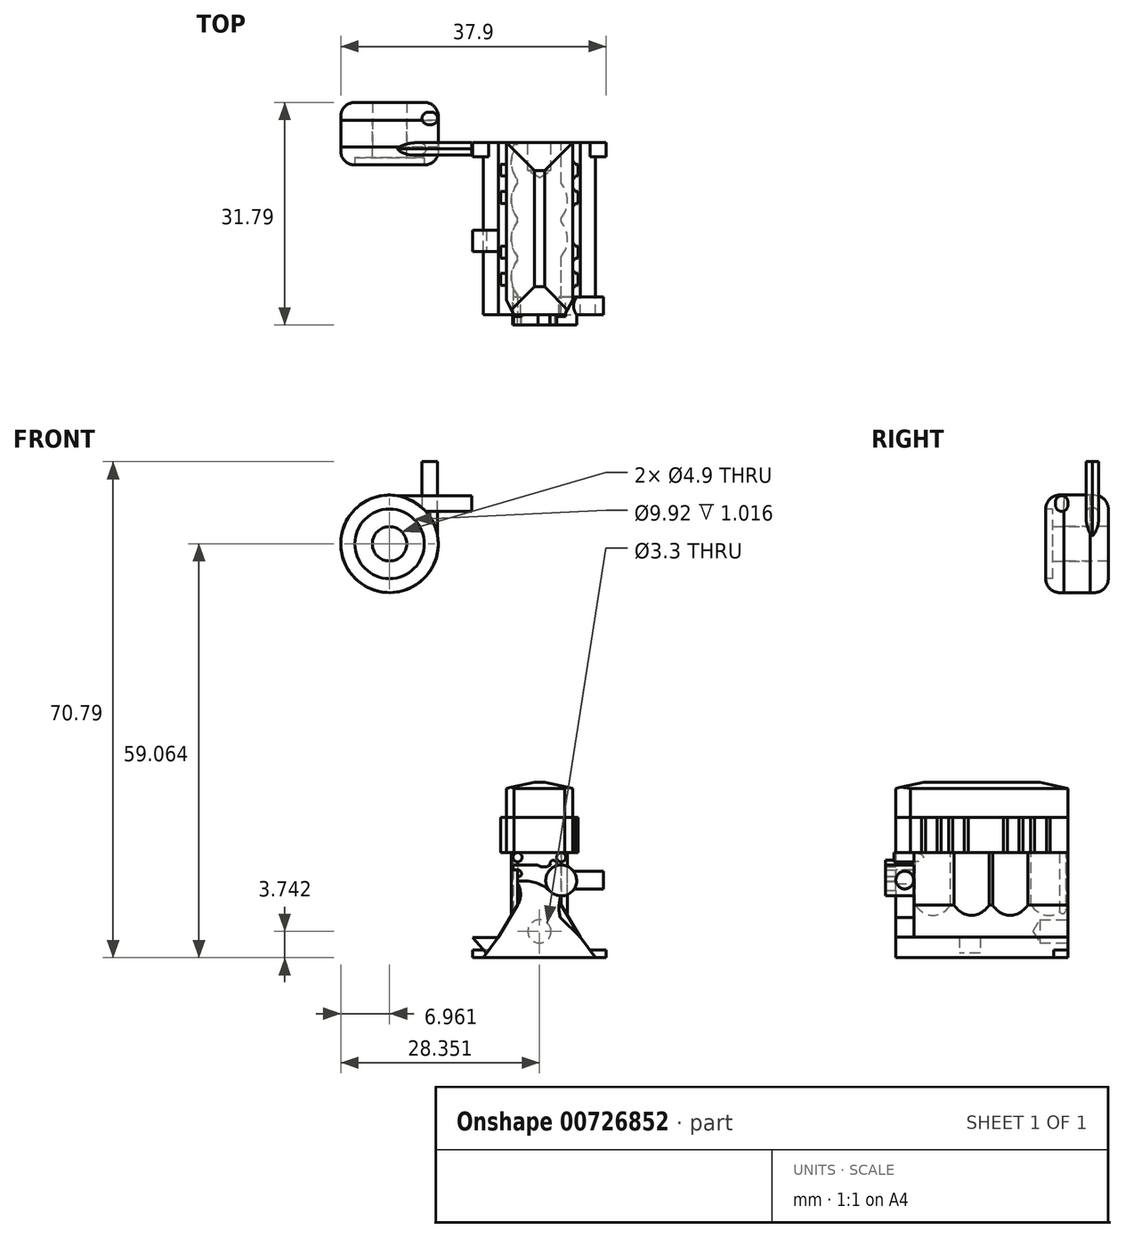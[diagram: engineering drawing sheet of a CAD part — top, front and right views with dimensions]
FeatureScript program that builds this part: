
annotation { "Feature Type Name" : "Feature", "Feature Type Description" : "" }
export const myFeature = defineFeature(function(context is Context, id is Id, definition is map)
    precondition{}
    {
        {
            var Q0;
            Q0=qCreatedBy(makeId("Front.planeOp"),FACE);
            var sketch = newSketch(context, id + "F0", { "sketchPlane" : qUnion([Q0])});
            skLineSegment(sketch, "E0.bottom", {"start": v(-2.64, 0.8) * mm, "end": v(3.58, 0.8) * mm});
            skLineSegment(sketch, "E0.top", {"start": v(-2.64, -6.71) * mm, "end": v(3.58, -6.71) * mm});
            skLineSegment(sketch, "E0.left", {"start": v(-2.64, 0.8) * mm, "end": v(-2.64, -6.71) * mm});
            skLineSegment(sketch, "E0.right", {"start": v(3.58, 0.8) * mm, "end": v(3.58, -6.71) * mm});
            skLineSegment(sketch, "E1", {"start": v(-2.64, -6.71) * mm, "end": v(-5.38, -11.28) * mm});
            skPoint(sketch, "E2", {"position": v(0.47, -6.71) * mm});
            skLineSegment(sketch, "E3.MirrorCS", {"start": v(3.58, -6.71) * mm, "end": v(6.32, -11.28) * mm});
            skLineSegment(sketch, "E4", {"start": v(-5.38, -11.28) * mm, "end": v(-7.54, -14.2) * mm});
            skLineSegment(sketch, "E5.MirrorCS", {"start": v(6.32, -11.28) * mm, "end": v(8.48, -14.2) * mm});
            skLineSegment(sketch, "E6", {"start": v(-7.54, -14.2) * mm, "end": v(8.48, -14.2) * mm});
            skLineSegment(sketch, "E7", {"start": v(7.69, -13.13) * mm, "end": v(10.02, -13.13) * mm});
            skLineSegment(sketch, "E8", {"start": v(10.02, -13.13) * mm, "end": v(10.02, -14.2) * mm});
            skLineSegment(sketch, "E9", {"start": v(10.02, -14.2) * mm, "end": v(8.48, -14.2) * mm});
            skLineSegment(sketch, "E10.MirrorCS", {"start": v(-6.74, -13.13) * mm, "end": v(-9.08, -13.13) * mm});
            skLineSegment(sketch, "E11.MirrorCS", {"start": v(-9.08, -13.13) * mm, "end": v(-9.08, -14.2) * mm});
            skLineSegment(sketch, "E12.MirrorCS", {"start": v(-9.08, -14.2) * mm, "end": v(-7.54, -14.2) * mm});
            skSolve(sketch);
        }
        {
            var Q0;
            Q0=makeQuery(id+"F0.imprint","IMPRINT",FACE,{"disambiguationData":[TD([[makeQuery(id+"F0.imprint","IMPRINT",EDGE,{"derivedFrom":sQuery(id+"F0.wireOp",EDGE,"E0.bottom")}),-1.0]])]});
            var Q1;
            Q1=makeQuery(id+"F0.imprint","IMPRINT",FACE,{"disambiguationData":[TD([[makeQuery(id+"F0.imprint","IMPRINT",EDGE,{"derivedFrom":sQuery(id+"F0.wireOp",EDGE,"E0.top")}),-1.0]])]});
            extrude(context, id + "F1", {"entities" : qUnion([Q0, Q1]), "depth" : 22 * mm, "offsetDistance" : 25.4 * mm});
        }
        {
            var Q0;
            {var subQ2=sQuery(id+"F0.wireOp",EDGE,"E7");Q0=makeQuery(id+"F0.imprint","IMPRINT",FACE,{"disambiguationData":[TD([[makeQuery(id+"F0.imprint","IMPRINT",EDGE,{"derivedFrom":subQ2}),-1.0]])]});}
            var Q1;
            {var subQ2=sQuery(id+"F0.wireOp",EDGE,"E10.MirrorCS");Q1=makeQuery(id+"F0.imprint","IMPRINT",FACE,{"disambiguationData":[TD([[makeQuery(id+"F0.imprint","IMPRINT",EDGE,{"derivedFrom":subQ2}),1.0]])]});}
            extrude(context, id + "F2", {"entities" : qUnion([Q0, Q1]), "operationType" : NewBodyOperationType.ADD, "depth" : 2 * mm, "offsetDistance" : 25.4 * mm});
        }
        {
            var Q0;
            Q0=makeQuery(id+"F1.opExtrude","SWEPT_FACE",FACE,{"disambiguationData":[OSD([sQuery(id+"F0.wireOp",EDGE,"E0.bottom")])]});
            var sketch = newSketch(context, id + "F3", { "sketchPlane" : qUnion([Q0])});
            skPoint(sketch, "E13", {"position": v(3.58, -11) * mm});
            skLineSegment(sketch, "E14", {"start": v(3.58, 0) * mm, "end": v(3.58, -11) * mm});
            skLineSegment(sketch, "E15", {"start": v(3.58, -11) * mm, "end": v(3.58, -22) * mm});
            skPoint(sketch, "E16", {"position": v(3.58, -16.5) * mm});
            skPoint(sketch, "E17", {"position": v(3.58, -5.5) * mm});
            skLineSegment(sketch, "E18", {"start": v(3.58, -5.5) * mm, "end": v(-2.64, -5.5) * mm});
            skLineSegment(sketch, "E19", {"start": v(-2.64, 0) * mm, "end": v(-2.64, -5.5) * mm});
            skLineSegment(sketch, "E20", {"start": v(-2.64, 0) * mm, "end": v(3.58, 0) * mm});
            skLineSegment(sketch, "E21", {"start": v(-2.64, -5.5) * mm, "end": v(-2.64, -22) * mm});
            skLineSegment(sketch, "E22", {"start": v(-2.64, -22) * mm, "end": v(3.58, -22) * mm});
            skLineSegment(sketch, "E23", {"start": v(3.58, -11) * mm, "end": v(-2.64, -11) * mm});
            skLineSegment(sketch, "E24", {"start": v(3.58, -16.5) * mm, "end": v(-2.64, -16.5) * mm});
            skPoint(sketch, "E25", {"position": v(0.47, -5.5) * mm});
            skLineSegment(sketch, "E26", {"start": v(0.47, 0) * mm, "end": v(0.47, -5.5) * mm});
            skLineSegment(sketch, "E27", {"start": v(0.47, -11) * mm, "end": v(0.47, -5.5) * mm});
            skLineSegment(sketch, "E28", {"start": v(0.47, -11) * mm, "end": v(0.47, -16.5) * mm});
            skLineSegment(sketch, "E29", {"start": v(0.47, -16.5) * mm, "end": v(0.47, -22) * mm});
            skPoint(sketch, "E30", {"position": v(0.47, -19.25) * mm});
            skPoint(sketch, "E31", {"position": v(0.47, -13.75) * mm});
            skPoint(sketch, "E32", {"position": v(0.47, -8.25) * mm});
            skPoint(sketch, "E33", {"position": v(0.47, -2.75) * mm});
            skArc(sketch, "E34", {"start": v(-2.43, 0) * mm, "mid": v(0.47, -6.75) * mm, "end": v(3.38, 0) * mm});
            skCircle(sketch, "E35", {"center": v(0.47, -8.25) * mm, "radius": 4 * mm});
            skCircle(sketch, "E36", {"center": v(0.47, -13.75) * mm, "radius": 4 * mm});
            skArc(sketch, "E37", {"start": v(3.38, -22) * mm, "mid": v(0.47, -15.25) * mm, "end": v(-2.43, -22) * mm});
            skPoint(sketch, "E38", {"position": v(3.58, -0.24) * mm});
            skPoint(sketch, "E39", {"position": v(3.58, -5.26) * mm});
            skPoint(sketch, "E40", {"position": v(-2.64, -5.26) * mm});
            skPoint(sketch, "E41", {"position": v(-2.64, -0.24) * mm});
            skPoint(sketch, "E42", {"position": v(-2.64, -5.74) * mm});
            skPoint(sketch, "E43", {"position": v(-2.64, -10.76) * mm});
            skArc(sketch, "E44", {"start": v(-2.64, -0.24) * mm, "mid": v(-3.37, -0.76) * mm, "end": v(-2.64, -1.27) * mm});
            skSolve(sketch);
        }
        {
            var Q0;
            {var subQ0=sQuery(id+"F3.wireOp",EDGE,"E34");var subQ1=sQuery(id+"F3.wireOp",EDGE,"E14");var subQ2=makeQuery(id+"F3.imprint","INTERSECT",VERTEX,{"disambiguationData":[OD(0.0)],"derivedFrom":[subQ1,subQ0]});Q0=makeQuery(id+"F3.imprint","IMPRINT",FACE,{"disambiguationData":[TD([[makeQuery(id+"F3.imprint","IMPRINT",EDGE,{"disambiguationData":[TD([[subQ2,-1.0]])],"derivedFrom":subQ1}),-1.0]])]});}
            var Q1;
            {var subQ0=sQuery(id+"F3.wireOp",EDGE,"E35");var subQ1=sQuery(id+"F3.wireOp",EDGE,"E14");var subQ2=makeQuery(id+"F3.imprint","INTERSECT",VERTEX,{"disambiguationData":[OD(0.0)],"derivedFrom":[subQ1,subQ0]});Q1=makeQuery(id+"F3.imprint","IMPRINT",FACE,{"disambiguationData":[TD([[makeQuery(id+"F3.imprint","IMPRINT",EDGE,{"disambiguationData":[TD([[subQ2,-1.0]])],"derivedFrom":subQ1}),-1.0]])]});}
            var Q2;
            {var subQ0=sQuery(id+"F3.wireOp",EDGE,"E36");var subQ1=sQuery(id+"F3.wireOp",EDGE,"E15");var subQ2=makeQuery(id+"F3.imprint","INTERSECT",VERTEX,{"disambiguationData":[OD(0.0)],"derivedFrom":[subQ1,subQ0]});Q2=makeQuery(id+"F3.imprint","IMPRINT",FACE,{"disambiguationData":[TD([[makeQuery(id+"F3.imprint","IMPRINT",EDGE,{"disambiguationData":[TD([[subQ2,-1.0]])],"derivedFrom":subQ1}),-1.0]])]});}
            var Q3;
            {var subQ0=sQuery(id+"F3.wireOp",EDGE,"E37");var subQ1=sQuery(id+"F3.wireOp",EDGE,"E15");var subQ2=makeQuery(id+"F3.imprint","INTERSECT",VERTEX,{"disambiguationData":[OD(0.0)],"derivedFrom":[subQ1,subQ0]});Q3=makeQuery(id+"F3.imprint","IMPRINT",FACE,{"disambiguationData":[TD([[makeQuery(id+"F3.imprint","IMPRINT",EDGE,{"disambiguationData":[TD([[subQ2,-1.0]])],"derivedFrom":subQ1}),-1.0]])]});}
            var Q4;
            {var subQ0=sQuery(id+"F3.wireOp",EDGE,"E37");var subQ1=sQuery(id+"F3.wireOp",EDGE,"E21");var subQ2=makeQuery(id+"F3.imprint","INTERSECT",VERTEX,{"disambiguationData":[OD(0.0)],"derivedFrom":[subQ1,subQ0]});Q4=makeQuery(id+"F3.imprint","IMPRINT",FACE,{"disambiguationData":[TD([[makeQuery(id+"F3.imprint","IMPRINT",EDGE,{"disambiguationData":[TD([[subQ2,-1.0]])],"derivedFrom":subQ1}),1.0]])]});}
            var Q5;
            {var subQ0=sQuery(id+"F3.wireOp",EDGE,"E36");var subQ1=sQuery(id+"F3.wireOp",EDGE,"E21");var subQ2=makeQuery(id+"F3.imprint","INTERSECT",VERTEX,{"disambiguationData":[OD(0.0)],"derivedFrom":[subQ1,subQ0]});Q5=makeQuery(id+"F3.imprint","IMPRINT",FACE,{"disambiguationData":[TD([[makeQuery(id+"F3.imprint","IMPRINT",EDGE,{"disambiguationData":[TD([[subQ2,-1.0]])],"derivedFrom":subQ1}),1.0]])]});}
            var Q6;
            {var subQ0=sQuery(id+"F3.wireOp",EDGE,"E35");var subQ1=sQuery(id+"F3.wireOp",EDGE,"E21");var subQ2=makeQuery(id+"F3.imprint","INTERSECT",VERTEX,{"disambiguationData":[OD(0.0)],"derivedFrom":[subQ1,subQ0]});Q6=makeQuery(id+"F3.imprint","IMPRINT",FACE,{"disambiguationData":[TD([[makeQuery(id+"F3.imprint","IMPRINT",EDGE,{"disambiguationData":[TD([[subQ2,-1.0]])],"derivedFrom":subQ1}),1.0]])]});}
            var Q7;
            {var subQ0=sQuery(id+"F3.wireOp",EDGE,"E34");var subQ1=sQuery(id+"F3.wireOp",EDGE,"E19");var subQ2=makeQuery(id+"F3.imprint","INTERSECT",VERTEX,{"disambiguationData":[OD(0.0)],"derivedFrom":[subQ1,subQ0]});Q7=makeQuery(id+"F3.imprint","IMPRINT",FACE,{"disambiguationData":[TD([[makeQuery(id+"F3.imprint","IMPRINT",EDGE,{"disambiguationData":[TD([[subQ2,-1.0]])],"derivedFrom":subQ1}),1.0]])]});}
            extrude(context, id + "F4", {"entities" : qUnion([Q0, Q1, Q2, Q3, Q4, Q5, Q6, Q7]), "operationType" : NewBodyOperationType.ADD, "oppositeDirection" : true, "depth" : 10 * mm, "offsetDistance" : 25.4 * mm});
        }
        {
            var Q0;
            Q0=makeQuery(id+"F1.opExtrude","CAP_FACE",FACE,{"disambiguationData":[OSD([sQuery(id+"F0.wireOp",EDGE,"E0.bottom"),sQuery(id+"F0.wireOp",EDGE,"E0.left"),sQuery(id+"F0.wireOp",EDGE,"E0.right"),sQuery(id+"F0.wireOp",EDGE,"E1"),sQuery(id+"F0.wireOp",EDGE,"E3.MirrorCS"),sQuery(id+"F0.wireOp",EDGE,"E4"),sQuery(id+"F0.wireOp",EDGE,"E5.MirrorCS"),sQuery(id+"F0.wireOp",EDGE,"E6")])],"isStart":false});
            var sketch = newSketch(context, id + "F5", { "sketchPlane" : qUnion([Q0])});
            skPoint(sketch, "E45", {"position": v(0.47, 0.8) * mm});
            skLineSegment(sketch, "E46", {"start": v(0.47, 0.8) * mm, "end": v(0.47, -1.26) * mm});
            skCircle(sketch, "E47", {"center": v(-2.64, 0.13) * mm, "radius": 0.65 * mm});
            skCircle(sketch, "E48.MirrorC", {"center": v(3.58, 0.13) * mm, "radius": 0.65 * mm});
            skSolve(sketch);
        }
        {
            var Q0;
            {var subQ0=sQuery(id+"F5.wireOp",EDGE,"E47");var subQ1=makeQuery(id+"F1.opExtrude","CAP_EDGE",EDGE,{"disambiguationData":[OSD([sQuery(id+"F0.wireOp",EDGE,"E0.left")])],"isStart":false});var subQ2=makeQuery(id+"F5.imprint","INTERSECT",VERTEX,{"disambiguationData":[OD(0.0)],"derivedFrom":[subQ1,subQ0]});Q0=makeQuery(id+"F5.imprint","IMPRINT",FACE,{"disambiguationData":[TD([[makeQuery(id+"F5.imprint","IMPRINT",EDGE,{"disambiguationData":[TD([[subQ2,-1.0]])],"derivedFrom":subQ0}),1.0]])]});}
            var Q1;
            {var subQ0=sQuery(id+"F5.wireOp",EDGE,"E48.MirrorC");var subQ1=makeQuery(id+"F1.opExtrude","CAP_EDGE",EDGE,{"disambiguationData":[OSD([sQuery(id+"F0.wireOp",EDGE,"E0.right")])],"isStart":false});var subQ2=makeQuery(id+"F5.imprint","INTERSECT",VERTEX,{"disambiguationData":[OD(0.0)],"derivedFrom":[subQ1,subQ0]});Q1=makeQuery(id+"F5.imprint","IMPRINT",FACE,{"disambiguationData":[TD([[makeQuery(id+"F5.imprint","IMPRINT",EDGE,{"disambiguationData":[TD([[subQ2,-1.0]])],"derivedFrom":subQ0}),-1.0]])]});}
            extrude(context, id + "F6", {"entities" : qUnion([Q0, Q1]), "operationType" : NewBodyOperationType.ADD, "oppositeDirection" : true, "depth" : 3 * mm, "offsetDistance" : 25.4 * mm});
        }
        {
            var Q0;
            {var subQ0=sQuery(id+"F3.wireOp",EDGE,"E44");var subQ1=sQuery(id+"F3.wireOp",EDGE,"E34");var subQ3=makeQuery(id+"F3.imprint","INTERSECT",VERTEX,{"derivedFrom":[subQ1,subQ0]});Q0=makeQuery(id+"F3.imprint","IMPRINT",FACE,{"disambiguationData":[TD([[makeQuery(id+"F3.imprint","IMPRINT",EDGE,{"disambiguationData":[TD([[subQ3,1.0]])],"derivedFrom":subQ1}),-1.0]])]});}
            var Q1;
            {var subQ0=sQuery(id+"F3.wireOp",EDGE,"E44");var subQ2=sQuery(id+"F3.wireOp",EDGE,"E19");var subQ4=makeQuery(id+"F3.imprint","INTERSECT",VERTEX,{"derivedFrom":[subQ2,subQ0]});Q1=makeQuery(id+"F3.imprint","IMPRINT",FACE,{"disambiguationData":[TD([[makeQuery(id+"F3.imprint","IMPRINT",EDGE,{"disambiguationData":[TD([[subQ4,1.0]])],"derivedFrom":subQ0}),1.0]])]});}
            extrude(context, id + "F7", {"entities" : qUnion([Q0, Q1]), "operationType" : NewBodyOperationType.ADD, "oppositeDirection" : true, "depth" : 9.5 * mm, "offsetDistance" : 25.4 * mm});
        }
        {
            var Q0;
            {var subQ0=sQuery(id+"F0.wireOp",EDGE,"E5.MirrorCS");var subQ1=sQuery(id+"F0.wireOp",EDGE,"E4");Q0=makeQuery(id+"F2.boolean.opBoolean","MERGE",FACE,{"derivedFrom":[makeQuery(id+"F1.opExtrude","CAP_FACE",FACE,{"disambiguationData":[OSD([sQuery(id+"F0.wireOp",EDGE,"E0.bottom"),sQuery(id+"F0.wireOp",EDGE,"E0.left"),sQuery(id+"F0.wireOp",EDGE,"E0.right"),sQuery(id+"F0.wireOp",EDGE,"E1"),sQuery(id+"F0.wireOp",EDGE,"E3.MirrorCS"),subQ1,subQ0,sQuery(id+"F0.wireOp",EDGE,"E6")])],"isStart":true}),makeQuery(id+"F2.opExtrude","CAP_FACE",FACE,{"disambiguationData":[OSD([subQ1,sQuery(id+"F0.wireOp",EDGE,"E10.MirrorCS"),sQuery(id+"F0.wireOp",EDGE,"E11.MirrorCS"),sQuery(id+"F0.wireOp",EDGE,"E12.MirrorCS")])],"isStart":true}),makeQuery(id+"F2.opExtrude","CAP_FACE",FACE,{"disambiguationData":[OSD([subQ0,sQuery(id+"F0.wireOp",EDGE,"E7"),sQuery(id+"F0.wireOp",EDGE,"E8"),sQuery(id+"F0.wireOp",EDGE,"E9")])],"isStart":true})]});}
            var sketch = newSketch(context, id + "F8", { "sketchPlane" : qUnion([Q0])});
            skLineSegment(sketch, "E49", {"start": v(-3.58, -6.71) * mm, "end": v(2.64, -6.71) * mm});
            skPoint(sketch, "E50", {"position": v(-0.47, -6.71) * mm});
            skLineSegment(sketch, "E51", {"start": v(-0.47, -6.71) * mm, "end": v(-0.47, -14.2) * mm});
            skPoint(sketch, "E52", {"position": v(-0.47, -10.46) * mm});
            skCircle(sketch, "E53", {"center": v(-0.47, -10.46) * mm, "radius": 2.45 * mm});
            skCircle(sketch, "E54", {"center": v(-0.47, -10.46) * mm, "radius": 1.7 * mm});
            skSolve(sketch);
        }
        {
            var Q0;
            Q0=sQuery(id+"F8.wireOp",VERTEX,"E52");
            var Q1;
            Q1=makeQuery(id+"F1.opExtrude","SWEPT_BODY",BODY,{"disambiguationData":[OSD([sQuery(id+"F0.wireOp",EDGE,"E0.bottom"),sQuery(id+"F0.wireOp",EDGE,"E0.left"),sQuery(id+"F0.wireOp",EDGE,"E0.right"),sQuery(id+"F0.wireOp",EDGE,"E1"),sQuery(id+"F0.wireOp",EDGE,"E3.MirrorCS"),sQuery(id+"F0.wireOp",EDGE,"E4"),sQuery(id+"F0.wireOp",EDGE,"E5.MirrorCS"),sQuery(id+"F0.wireOp",EDGE,"E6")])]});
            hole(context, id + "F9", {"style" : HoleStyle.SIMPLE, "endStyle" : HoleEndStyle.BLIND, "holeDiameter" : 3.3 * mm, "majorDiameter" : 6.35 * mm, "holeDepth" : 4 * mm, "isTappedThrough" : true, "tappedDepth" : 12.7 * mm, "tapClearance" : 3, "locations" : qUnion([Q0]), "scope" : qUnion([Q1])});
        }
        {
            var Q0;
            Q0=qCreatedBy(makeId("Front.planeOp"),FACE);
            var sketch = newSketch(context, id + "F10", { "sketchPlane" : qUnion([Q0])});
            skCircle(sketch, "E55", {"center": v(-20.92, 44.86) * mm, "radius": 2.45 * mm});
            skCircle(sketch, "E56", {"center": v(-20.92, 44.86) * mm, "radius": 6.96 * mm});
            skLineSegment(sketch, "E57", {"start": v(-19.74, 51.72) * mm, "end": v(-9.2, 51.72) * mm});
            skLineSegment(sketch, "E58", {"start": v(-9.2, 51.72) * mm, "end": v(-9.2, 49.5) * mm});
            skLineSegment(sketch, "E59", {"start": v(-9.2, 49.5) * mm, "end": v(-15.73, 49.5) * mm});
            skLineSegment(sketch, "E60", {"start": v(-20.92, 44.86) * mm, "end": v(-20.92, 47.31) * mm});
            skPoint(sketch, "E61", {"position": v(-27.88, 44.86) * mm});
            skSolve(sketch);
        }
        {
            var Q0;
            Q0=makeQuery(id+"F10.imprint","IMPRINT",FACE,{"disambiguationData":[TD([[makeQuery(id+"F10.imprint","IMPRINT",EDGE,{"derivedFrom":sQuery(id+"F10.wireOp",EDGE,"E55")}),-1.0]])]});
            extrude(context, id + "F11", {"entities" : qUnion([Q0]), "endBound" : BoundingType.SYMMETRIC, "depth" : 6.35 * mm, "offsetDistance" : 25.4 * mm});
        }
        {
            var Q0;
            {var subQ0=sQuery(id+"F10.wireOp",EDGE,"E57");Q0=makeQuery(id+"F10.imprint","IMPRINT",FACE,{"disambiguationData":[TD([[makeQuery(id+"F10.imprint","IMPRINT",EDGE,{"derivedFrom":subQ0}),-1.0]])]});}
            extrude(context, id + "F12", {"entities" : qUnion([Q0]), "operationType" : NewBodyOperationType.ADD, "depth" : 1.78 * mm, "offsetDistance" : 25.4 * mm});
        }
        {
            var Q0;
            Q0=makeQuery(id+"F11.opExtrude","CAP_EDGE",EDGE,{"disambiguationData":[OSD([sQuery(id+"F10.wireOp",EDGE,"E56")])],"isStart":false});
            fillet(context, id + "F13", {"entities" : qUnion([Q0]), "radius" : 2 * mm, "tangentPropagation" : true, "allowEdgeOverflow" : false});
        }
        {
            var Q0;
            Q0=makeQuery(id+"F12.opExtrude","CAP_EDGE",EDGE,{"disambiguationData":[OSD([sQuery(id+"F10.wireOp",EDGE,"E57")])],"isStart":false});
            var Q1;
            Q1=makeQuery(id+"F12.opExtrude","CAP_EDGE",EDGE,{"disambiguationData":[OSD([sQuery(id+"F10.wireOp",EDGE,"E59")])],"isStart":false});
            var Q2;
            Q2=makeQuery(id+"F12.opExtrude","CAP_EDGE",EDGE,{"disambiguationData":[OSD([sQuery(id+"F10.wireOp",EDGE,"E57")])],"isStart":true});
            var Q3;
            Q3=makeQuery(id+"F12.opExtrude","CAP_EDGE",EDGE,{"disambiguationData":[OSD([sQuery(id+"F10.wireOp",EDGE,"E59")])],"isStart":true});
            fillet(context, id + "F14", {"entities" : qUnion([Q0, Q1, Q2, Q3]), "radius" : .9 * mm, "tangentPropagation" : true, "allowEdgeOverflow" : false});
        }
        {
            var Q0;
            Q0=makeQuery(id+"F11.opExtrude","SWEPT_BODY",BODY,{"disambiguationData":[OSD([sQuery(id+"F10.wireOp",EDGE,"E55"),sQuery(id+"F10.wireOp",EDGE,"E56")])]});
            transform(context, id + "F15", {"entities" : qUnion([Q0]), "transformType" : TransformType.TRANSLATION_3D, "dx" : 0 * mm, "dy" : 10.77 * mm, "dz" : 0 * mm, "makeCopy" : true});
        }
        {
            var Q0;
            Q0=makeQuery(id+"F15.opPattern","COPY",BODY,{"derivedFrom":makeQuery(id+"F11.opExtrude","SWEPT_BODY",BODY,{"disambiguationData":[OSD([sQuery(id+"F10.wireOp",EDGE,"E55"),sQuery(id+"F10.wireOp",EDGE,"E56")])]}),"instanceName":"1"});
            var Q1;
            Q1=sQuery(id+"F10.wireOp",EDGE,"E55");
            transform(context, id + "F16", {"entities" : qUnion([Q0]), "transformType" : TransformType.ROTATION, "transformAxis" : qUnion([Q1]), "angle" : 90 * degree, "makeCopy" : false});
        }
        {
            var Q0;
            Q0=makeQuery(id+"F15.opPattern","COPY",BODY,{"derivedFrom":makeQuery(id+"F11.opExtrude","SWEPT_BODY",BODY,{"disambiguationData":[OSD([sQuery(id+"F10.wireOp",EDGE,"E55"),sQuery(id+"F10.wireOp",EDGE,"E56")])]}),"instanceName":"1"});
            var Q1;
            Q1=sQuery(id+"F10.wireOp",EDGE,"E60");
            transform(context, id + "F17", {"entities" : qUnion([Q0]), "transformType" : TransformType.ROTATION, "transformAxis" : qUnion([Q1]), "angle" : 180 * degree, "oppositeDirection" : true, "makeCopy" : false});
        }
        {
            var Q0;
            Q0=makeQuery(id+"F15.opPattern","COPY",BODY,{"derivedFrom":makeQuery(id+"F11.opExtrude","SWEPT_BODY",BODY,{"disambiguationData":[OSD([sQuery(id+"F10.wireOp",EDGE,"E55"),sQuery(id+"F10.wireOp",EDGE,"E56")])]}),"instanceName":"1"});
            transform(context, id + "F18", {"entities" : qUnion([Q0]), "transformType" : TransformType.TRANSLATION_3D, "dx" : 0 * mm, "dy" : 13.36 * mm, "dz" : 0 * mm, "makeCopy" : false});
        }
        {
            var Q0;
            Q0=makeQuery(id+"F11.opExtrude","CAP_FACE",FACE,{"disambiguationData":[OSD([sQuery(id+"F10.wireOp",EDGE,"E55"),sQuery(id+"F10.wireOp",EDGE,"E56")])],"isStart":false});
            extrude(context, id + "F19", {"entities" : qUnion([Q0]), "operationType" : NewBodyOperationType.REMOVE, "oppositeDirection" : true, "depth" : 1.02 * mm, "offsetDistance" : 25.4 * mm});
        }
        {
            var Q0;
            {var subQ0=sQuery(id+"F0.wireOp",EDGE,"E0.right");var subQ1=sQuery(id+"F0.wireOp",EDGE,"E0.left");Q0=makeQuery(id+"F6.boolean.opBoolean","MERGE",FACE,{"derivedFrom":[makeQuery(id+"F1.opExtrude","CAP_FACE",FACE,{"disambiguationData":[OSD([sQuery(id+"F0.wireOp",EDGE,"E0.bottom"),subQ1,subQ0,sQuery(id+"F0.wireOp",EDGE,"E1"),sQuery(id+"F0.wireOp",EDGE,"E3.MirrorCS"),sQuery(id+"F0.wireOp",EDGE,"E4"),sQuery(id+"F0.wireOp",EDGE,"E5.MirrorCS"),sQuery(id+"F0.wireOp",EDGE,"E6")])],"isStart":false}),makeQuery(id+"F6.opExtrude","CAP_FACE",FACE,{"disambiguationData":[OSD([subQ1,sQuery(id+"F5.wireOp",EDGE,"E47")])],"isStart":true}),makeQuery(id+"F6.opExtrude","CAP_FACE",FACE,{"disambiguationData":[OSD([subQ0,sQuery(id+"F5.wireOp",EDGE,"E48.MirrorC")])],"isStart":true})]});}
            cPlane(context, id + "F20", {"entities" : qUnion([Q0]), "cplaneType" : CPlaneType.OFFSET, "offset" : 8 * mm, "oppositeDirection" : true, "width" : 152.4 * mm, "height" : 152.4 * mm});
        }
        {
            var Q0;
            Q0=qCreatedBy(id+"F20.planeOp",FACE);
            var sketch = newSketch(context, id + "F21", { "sketchPlane" : qUnion([Q0])});
            skLineSegment(sketch, "E62", {"start": v(-5.34, -11.3) * mm, "end": v(-9.03, -11.3) * mm});
            skLineSegment(sketch, "E63", {"start": v(-9.03, -11.3) * mm, "end": v(-7.07, -13.6) * mm});
            skLineSegment(sketch, "E64", {"start": v(-7.07, -13.6) * mm, "end": v(-5.34, -11.3) * mm});
            skSolve(sketch);
        }
        {
            var Q0;
            Q0=makeQuery(id+"F21.imprint","IMPRINT",FACE,{"disambiguationData":[TD([[makeQuery(id+"F21.imprint","IMPRINT",EDGE,{"derivedFrom":sQuery(id+"F21.wireOp",EDGE,"E62")}),1.0]])]});
            extrude(context, id + "F22", {"entities" : qUnion([Q0]), "operationType" : NewBodyOperationType.ADD, "endBound" : BoundingType.SYMMETRIC, "depth" : 3 * mm, "offsetDistance" : 25.4 * mm});
        }
        {
            var Q0;
            {var subQ0=sQuery(id+"F0.wireOp",EDGE,"E0.right");var subQ1=sQuery(id+"F0.wireOp",EDGE,"E0.left");Q0=makeQuery(id+"F6.boolean.opBoolean","MERGE",FACE,{"derivedFrom":[makeQuery(id+"F1.opExtrude","CAP_FACE",FACE,{"disambiguationData":[OSD([sQuery(id+"F0.wireOp",EDGE,"E0.bottom"),subQ1,subQ0,sQuery(id+"F0.wireOp",EDGE,"E1"),sQuery(id+"F0.wireOp",EDGE,"E3.MirrorCS"),sQuery(id+"F0.wireOp",EDGE,"E4"),sQuery(id+"F0.wireOp",EDGE,"E5.MirrorCS"),sQuery(id+"F0.wireOp",EDGE,"E6")])],"isStart":false}),makeQuery(id+"F6.opExtrude","CAP_FACE",FACE,{"disambiguationData":[OSD([subQ1,sQuery(id+"F5.wireOp",EDGE,"E47")])],"isStart":true}),makeQuery(id+"F6.opExtrude","CAP_FACE",FACE,{"disambiguationData":[OSD([subQ0,sQuery(id+"F5.wireOp",EDGE,"E48.MirrorC")])],"isStart":true})]});}
            var sketch = newSketch(context, id + "F23", { "sketchPlane" : qUnion([Q0])});
            skPoint(sketch, "E65", {"position": v(0.47, 0.8) * mm});
            skPoint(sketch, "E66", {"position": v(0.47, -1.12) * mm});
            skLineSegment(sketch, "E67", {"start": v(0.47, 0.8) * mm, "end": v(0.47, -1.12) * mm});
            skSolve(sketch);
        }
        {
            var Q0;
            Q0=sQuery(id+"F23.wireOp",EDGE,"E67");
            cPlane(context, id + "F24", {"entities" : qUnion([Q0]), "cplaneType" : CPlaneType.LINE_ANGLE, "offset" : 25.4 * mm, "angle" : 0 * degree, "width" : 152.4 * mm, "height" : 152.4 * mm});
        }
        {
            var Q0;
            {var subQ0=sQuery(id+"F3.wireOp",EDGE,"E44");var subQ1=sQuery(id+"F3.wireOp",EDGE,"E19");var subQ2=sQuery(id+"F3.wireOp",EDGE,"E35");var subQ3=sQuery(id+"F3.wireOp",EDGE,"E21");var subQ4=sQuery(id+"F3.wireOp",EDGE,"E36");var subQ5=sQuery(id+"F3.wireOp",EDGE,"E37");var subQ6=sQuery(id+"F3.wireOp",EDGE,"E34");var subQ7=sQuery(id+"F3.wireOp",EDGE,"E15");var subQ8=sQuery(id+"F3.wireOp",EDGE,"E14");Q0=makeQuery(id+"F7.boolean.opBoolean","MERGE",FACE,{"derivedFrom":[makeQuery(id+"F4.boolean.opBoolean","MERGE",FACE,{"derivedFrom":[makeQuery(id+"F1.opExtrude","SWEPT_FACE",FACE,{"disambiguationData":[OSD([sQuery(id+"F0.wireOp",EDGE,"E0.bottom")])]}),makeQuery(id+"F4.opExtrude","CAP_FACE",FACE,{"disambiguationData":[OSD([subQ8,subQ2])],"isStart":true}),makeQuery(id+"F4.opExtrude","CAP_FACE",FACE,{"disambiguationData":[OSD([subQ8,subQ6])],"isStart":true}),makeQuery(id+"F4.opExtrude","CAP_FACE",FACE,{"disambiguationData":[OSD([subQ7,subQ5])],"isStart":true}),makeQuery(id+"F4.opExtrude","CAP_FACE",FACE,{"disambiguationData":[OSD([subQ7,subQ4])],"isStart":true}),makeQuery(id+"F4.opExtrude","CAP_FACE",FACE,{"disambiguationData":[OSD([subQ1,subQ6,subQ0])],"isStart":true}),makeQuery(id+"F4.opExtrude","CAP_FACE",FACE,{"disambiguationData":[OSD([subQ3,subQ5])],"isStart":true}),makeQuery(id+"F4.opExtrude","CAP_FACE",FACE,{"disambiguationData":[OSD([subQ3,subQ4])],"isStart":true}),makeQuery(id+"F4.opExtrude","CAP_FACE",FACE,{"disambiguationData":[OSD([subQ3,subQ2])],"isStart":true})]}),makeQuery(id+"F7.opExtrude","CAP_FACE",FACE,{"disambiguationData":[OSD([subQ1,subQ0])],"isStart":true})]});}
            var sketch = newSketch(context, id + "F25", { "sketchPlane" : qUnion([Q0])});
            skLineSegment(sketch, "E68", {"start": v(5.2, -22.48) * mm, "end": v(5.2, 0) * mm});
            skPoint(sketch, "E69", {"position": v(3.58, 0) * mm});
            skPoint(sketch, "E70", {"position": v(-2.64, 0) * mm});
            skPoint(sketch, "E71", {"position": v(-4.26, 0) * mm});
            skLineSegment(sketch, "E72", {"start": v(5.2, 0) * mm, "end": v(-4.26, 0) * mm});
            skLineSegment(sketch, "E73", {"start": v(-4.26, 0) * mm, "end": v(-4.26, -22.48) * mm});
            skLineSegment(sketch, "E74", {"start": v(-4.26, -22.48) * mm, "end": v(-3.17, -24.57) * mm});
            skLineSegment(sketch, "E75.MirrorCS", {"start": v(5.2, -22.48) * mm, "end": v(4.11, -24.57) * mm});
            skLineSegment(sketch, "E76", {"start": v(4.11, -24.57) * mm, "end": v(-3.17, -24.57) * mm});
            skPoint(sketch, "E77.start.orphan", {"position": v(0.47, -22) * mm});
            skArc(sketch, "E78", {"start": v(5.2, -20.9) * mm, "mid": v(5.78, -19.5) * mm, "end": v(5.2, -18.1) * mm});
            skArc(sketch, "E79", {"start": v(5.2, -17) * mm, "mid": v(5.79, -15.61) * mm, "end": v(5.2, -14.21) * mm});
            skPoint(sketch, "E80", {"position": v(5.2, -9.2) * mm});
            skPoint(sketch, "E81", {"position": v(5.2, -6.4) * mm});
            skPoint(sketch, "E82", {"position": v(5.2, -5.31) * mm});
            skPoint(sketch, "E83", {"position": v(5.2, -2.52) * mm});
            skArc(sketch, "E84", {"start": v(5.2, -5.31) * mm, "mid": v(5.79, -3.91) * mm, "end": v(5.2, -2.52) * mm});
            skArc(sketch, "E85", {"start": v(5.2, -9.2) * mm, "mid": v(5.79, -7.8) * mm, "end": v(5.2, -6.4) * mm});
            skLineSegment(sketch, "E86", {"start": v(0.47, -22) * mm, "end": v(0.47, -21.08) * mm});
            skArc(sketch, "E87.MirrorCS", {"start": v(-4.26, -20.9) * mm, "mid": v(-4.84, -19.5) * mm, "end": v(-4.26, -18.1) * mm});
            skArc(sketch, "E88.MirrorCS", {"start": v(-4.26, -17) * mm, "mid": v(-4.85, -15.61) * mm, "end": v(-4.26, -14.21) * mm});
            skArc(sketch, "E89.MirrorCS", {"start": v(-4.26, -9.2) * mm, "mid": v(-4.85, -7.8) * mm, "end": v(-4.26, -6.4) * mm});
            skArc(sketch, "E90.MirrorCS", {"start": v(-4.26, -5.31) * mm, "mid": v(-4.85, -3.91) * mm, "end": v(-4.26, -2.52) * mm});
            skSolve(sketch);
        }
        {
            var Q0;
            {var subQ1=sQuery(id+"F25.wireOp",EDGE,"E74");Q0=makeQuery(id+"F25.imprint","IMPRINT",FACE,{"disambiguationData":[TD([[makeQuery(id+"F25.imprint","IMPRINT",EDGE,{"derivedFrom":subQ1}),1.0]])]});}
            var Q1;
            {var subQ0=sQuery(id+"F25.wireOp",EDGE,"E85");Q1=makeQuery(id+"F25.imprint","IMPRINT",FACE,{"disambiguationData":[TD([[makeQuery(id+"F25.imprint","IMPRINT",EDGE,{"derivedFrom":subQ0}),1.0]])]});}
            var Q2;
            {var subQ0=sQuery(id+"F25.wireOp",EDGE,"E84");Q2=makeQuery(id+"F25.imprint","IMPRINT",FACE,{"disambiguationData":[TD([[makeQuery(id+"F25.imprint","IMPRINT",EDGE,{"derivedFrom":subQ0}),1.0]])]});}
            var Q3;
            {var subQ0=sQuery(id+"F25.wireOp",EDGE,"E90.MirrorCS");Q3=makeQuery(id+"F25.imprint","IMPRINT",FACE,{"disambiguationData":[TD([[makeQuery(id+"F25.imprint","IMPRINT",EDGE,{"derivedFrom":subQ0}),-1.0]])]});}
            var Q4;
            {var subQ0=sQuery(id+"F25.wireOp",EDGE,"E89.MirrorCS");Q4=makeQuery(id+"F25.imprint","IMPRINT",FACE,{"disambiguationData":[TD([[makeQuery(id+"F25.imprint","IMPRINT",EDGE,{"derivedFrom":subQ0}),-1.0]])]});}
            var Q5;
            {var subQ0=sQuery(id+"F25.wireOp",EDGE,"E88.MirrorCS");Q5=makeQuery(id+"F25.imprint","IMPRINT",FACE,{"disambiguationData":[TD([[makeQuery(id+"F25.imprint","IMPRINT",EDGE,{"derivedFrom":subQ0}),-1.0]])]});}
            var Q6;
            {var subQ0=sQuery(id+"F25.wireOp",EDGE,"E87.MirrorCS");Q6=makeQuery(id+"F25.imprint","IMPRINT",FACE,{"disambiguationData":[TD([[makeQuery(id+"F25.imprint","IMPRINT",EDGE,{"derivedFrom":subQ0}),-1.0]])]});}
            var Q7;
            {var subQ0=sQuery(id+"F25.wireOp",EDGE,"E78");Q7=makeQuery(id+"F25.imprint","IMPRINT",FACE,{"disambiguationData":[TD([[makeQuery(id+"F25.imprint","IMPRINT",EDGE,{"derivedFrom":subQ0}),1.0]])]});}
            var Q8;
            {var subQ0=sQuery(id+"F25.wireOp",EDGE,"E79");Q8=makeQuery(id+"F25.imprint","IMPRINT",FACE,{"disambiguationData":[TD([[makeQuery(id+"F25.imprint","IMPRINT",EDGE,{"derivedFrom":subQ0}),1.0]])]});}
            var Q9;
            {var subQ7=sQuery(id+"F3.wireOp",EDGE,"E44");Q9=makeQuery(id+"F25.imprint","IMPRINT",FACE,{"disambiguationData":[TD([[makeQuery(id+"F25.imprint","IMPRINT",EDGE,{"derivedFrom":makeQuery(id+"F7.opExtrude","CAP_EDGE",EDGE,{"disambiguationData":[OSD([subQ7])],"isStart":true})}),1.0]])]});}
            extrude(context, id + "F26", {"entities" : qUnion([Q0, Q1, Q2, Q3, Q4, Q5, Q6, Q7, Q8, Q9]), "depth" : 5 * mm, "offsetDistance" : 25.4 * mm});
        }
        {
            var Q0;
            Q0=makeQuery(id+"F26.opExtrude","CAP_FACE",FACE,{"disambiguationData":[OSD([sQuery(id+"F25.wireOp",EDGE,"E68"),sQuery(id+"F25.wireOp",EDGE,"E72"),sQuery(id+"F25.wireOp",EDGE,"E73"),sQuery(id+"F25.wireOp",EDGE,"E74"),sQuery(id+"F25.wireOp",EDGE,"E75.MirrorCS"),sQuery(id+"F25.wireOp",EDGE,"E76"),sQuery(id+"F25.wireOp",EDGE,"E78"),sQuery(id+"F25.wireOp",EDGE,"E79"),sQuery(id+"F25.wireOp",EDGE,"E84"),sQuery(id+"F25.wireOp",EDGE,"E85"),sQuery(id+"F25.wireOp",EDGE,"E87.MirrorCS"),sQuery(id+"F25.wireOp",EDGE,"E88.MirrorCS"),sQuery(id+"F25.wireOp",EDGE,"E89.MirrorCS"),sQuery(id+"F25.wireOp",EDGE,"E90.MirrorCS")])],"isStart":false});
            var sketch = newSketch(context, id + "F27", { "sketchPlane" : qUnion([Q0])});
            skLineSegment(sketch, "E91", {"start": v(5.2, -17) * mm, "end": v(5.2, -14.21) * mm});
            skPoint(sketch, "E92", {"position": v(5.2, -16.45) * mm});
            skPoint(sketch, "E93", {"position": v(5.2, -14.77) * mm});
            skLineSegment(sketch, "E94", {"start": v(5.2, -16.45) * mm, "end": v(5.2, -14.77) * mm});
            skLineSegment(sketch, "E95", {"start": v(6, -14.77) * mm, "end": v(6, -16.45) * mm});
            skLineSegment(sketch, "E96", {"start": v(6, -16.45) * mm, "end": v(5.2, -16.45) * mm});
            skLineSegment(sketch, "E97", {"start": v(6, -14.77) * mm, "end": v(5.2, -14.77) * mm});
            skLineSegment(sketch, "E98", {"start": v(5.2, -18.1) * mm, "end": v(5.2, -20.9) * mm});
            skLineSegment(sketch, "E99", {"start": v(6, -20.34) * mm, "end": v(6, -18.66) * mm});
            skPoint(sketch, "E100", {"position": v(5.2, -18.66) * mm});
            skPoint(sketch, "E101", {"position": v(5.2, -20.34) * mm});
            skLineSegment(sketch, "E102", {"start": v(5.2, -20.34) * mm, "end": v(6, -20.34) * mm});
            skLineSegment(sketch, "E103", {"start": v(5.2, -18.66) * mm, "end": v(6, -18.66) * mm});
            skLineSegment(sketch, "E104", {"start": v(5.2, -9.2) * mm, "end": v(5.2, -6.4) * mm});
            skLineSegment(sketch, "E105", {"start": v(5.2, -5.31) * mm, "end": v(5.2, -2.52) * mm});
            skPoint(sketch, "E106", {"position": v(5.2, -3.08) * mm});
            skPoint(sketch, "E107", {"position": v(5.2, -4.75) * mm});
            skPoint(sketch, "E108", {"position": v(5.2, -6.96) * mm});
            skPoint(sketch, "E109", {"position": v(5.2, -8.64) * mm});
            skLineSegment(sketch, "E110", {"start": v(5.2, -8.64) * mm, "end": v(6, -8.64) * mm});
            skLineSegment(sketch, "E111", {"start": v(6, -8.64) * mm, "end": v(6, -6.96) * mm});
            skLineSegment(sketch, "E112", {"start": v(6, -6.96) * mm, "end": v(5.2, -6.96) * mm});
            skLineSegment(sketch, "E113", {"start": v(5.2, -4.75) * mm, "end": v(6, -4.75) * mm});
            skLineSegment(sketch, "E114", {"start": v(6, -4.75) * mm, "end": v(6, -3.08) * mm});
            skLineSegment(sketch, "E115", {"start": v(6, -3.08) * mm, "end": v(5.2, -3.08) * mm});
            skLineSegment(sketch, "E116", {"start": v(0.47, -24.57) * mm, "end": v(0.47, -23.27) * mm});
            skLineSegment(sketch, "E117.MirrorCS", {"start": v(-5.06, -20.34) * mm, "end": v(-5.06, -18.66) * mm});
            skLineSegment(sketch, "E118.MirrorCS", {"start": v(-4.26, -18.66) * mm, "end": v(-5.06, -18.66) * mm});
            skLineSegment(sketch, "E119.MirrorCS", {"start": v(-4.26, -20.34) * mm, "end": v(-5.06, -20.34) * mm});
            skLineSegment(sketch, "E120.MirrorCS", {"start": v(-5.06, -16.45) * mm, "end": v(-4.26, -16.45) * mm});
            skLineSegment(sketch, "E121.MirrorCS", {"start": v(-5.06, -14.77) * mm, "end": v(-5.06, -16.45) * mm});
            skLineSegment(sketch, "E122.MirrorCS", {"start": v(-5.06, -14.77) * mm, "end": v(-4.26, -14.77) * mm});
            skLineSegment(sketch, "E123.MirrorCS", {"start": v(-5.06, -6.96) * mm, "end": v(-4.26, -6.96) * mm});
            skLineSegment(sketch, "E124.MirrorCS", {"start": v(-4.26, -8.64) * mm, "end": v(-5.06, -8.64) * mm});
            skLineSegment(sketch, "E125.MirrorCS", {"start": v(-5.06, -8.64) * mm, "end": v(-5.06, -6.96) * mm});
            skLineSegment(sketch, "E126.MirrorCS", {"start": v(-4.26, -4.75) * mm, "end": v(-5.06, -4.75) * mm});
            skLineSegment(sketch, "E127.MirrorCS", {"start": v(-5.06, -4.75) * mm, "end": v(-5.06, -3.08) * mm});
            skLineSegment(sketch, "E128.MirrorCS", {"start": v(-5.06, -3.08) * mm, "end": v(-4.26, -3.08) * mm});
            skSolve(sketch);
        }
        {
            var Q0;
            {var subQ0=sQuery(id+"F27.wireOp",EDGE,"E114");Q0=makeQuery(id+"F27.imprint","IMPRINT",FACE,{"disambiguationData":[TD([[makeQuery(id+"F27.imprint","IMPRINT",EDGE,{"derivedFrom":subQ0}),1.0]])]});}
            var Q1;
            {var subQ0=sQuery(id+"F27.wireOp",EDGE,"E111");Q1=makeQuery(id+"F27.imprint","IMPRINT",FACE,{"disambiguationData":[TD([[makeQuery(id+"F27.imprint","IMPRINT",EDGE,{"derivedFrom":subQ0}),1.0]])]});}
            var Q2;
            {var subQ0=sQuery(id+"F27.wireOp",EDGE,"E95");Q2=makeQuery(id+"F27.imprint","IMPRINT",FACE,{"disambiguationData":[TD([[makeQuery(id+"F27.imprint","IMPRINT",EDGE,{"derivedFrom":subQ0}),-1.0]])]});}
            var Q3;
            {var subQ0=sQuery(id+"F27.wireOp",EDGE,"E99");Q3=makeQuery(id+"F27.imprint","IMPRINT",FACE,{"disambiguationData":[TD([[makeQuery(id+"F27.imprint","IMPRINT",EDGE,{"derivedFrom":subQ0}),1.0]])]});}
            var Q4;
            {var subQ0=sQuery(id+"F27.wireOp",EDGE,"E117.MirrorCS");Q4=makeQuery(id+"F27.imprint","IMPRINT",FACE,{"disambiguationData":[TD([[makeQuery(id+"F27.imprint","IMPRINT",EDGE,{"derivedFrom":subQ0}),-1.0]])]});}
            var Q5;
            {var subQ0=sQuery(id+"F27.wireOp",EDGE,"E121.MirrorCS");Q5=makeQuery(id+"F27.imprint","IMPRINT",FACE,{"disambiguationData":[TD([[makeQuery(id+"F27.imprint","IMPRINT",EDGE,{"derivedFrom":subQ0}),1.0]])]});}
            var Q6;
            {var subQ0=sQuery(id+"F27.wireOp",EDGE,"E125.MirrorCS");Q6=makeQuery(id+"F27.imprint","IMPRINT",FACE,{"disambiguationData":[TD([[makeQuery(id+"F27.imprint","IMPRINT",EDGE,{"derivedFrom":subQ0}),-1.0]])]});}
            var Q7;
            {var subQ0=sQuery(id+"F27.wireOp",EDGE,"E127.MirrorCS");Q7=makeQuery(id+"F27.imprint","IMPRINT",FACE,{"disambiguationData":[TD([[makeQuery(id+"F27.imprint","IMPRINT",EDGE,{"derivedFrom":subQ0}),-1.0]])]});}
            extrude(context, id + "F28", {"entities" : qUnion([Q0, Q1, Q2, Q3, Q4, Q5, Q6, Q7]), "operationType" : NewBodyOperationType.ADD, "oppositeDirection" : true, "depth" : 5 * mm, "offsetDistance" : 25.4 * mm});
        }
        {
            var Q0;
            {var subQ0=sQuery(id+"F25.wireOp",EDGE,"E90.MirrorCS");var subQ1=sQuery(id+"F25.wireOp",EDGE,"E89.MirrorCS");var subQ2=sQuery(id+"F25.wireOp",EDGE,"E88.MirrorCS");var subQ3=sQuery(id+"F25.wireOp",EDGE,"E87.MirrorCS");var subQ4=sQuery(id+"F25.wireOp",EDGE,"E84");var subQ5=sQuery(id+"F25.wireOp",EDGE,"E85");var subQ6=sQuery(id+"F25.wireOp",EDGE,"E78");var subQ7=sQuery(id+"F25.wireOp",EDGE,"E79");Q0=makeQuery(id+"F28.boolean.opBoolean","MERGE",FACE,{"derivedFrom":[makeQuery(id+"F26.opExtrude","CAP_FACE",FACE,{"disambiguationData":[OSD([sQuery(id+"F25.wireOp",EDGE,"E68"),sQuery(id+"F25.wireOp",EDGE,"E72"),sQuery(id+"F25.wireOp",EDGE,"E73"),sQuery(id+"F25.wireOp",EDGE,"E74"),sQuery(id+"F25.wireOp",EDGE,"E75.MirrorCS"),sQuery(id+"F25.wireOp",EDGE,"E76"),subQ6,subQ7,subQ4,subQ5,subQ3,subQ2,subQ1,subQ0])],"isStart":false}),makeQuery(id+"F28.opExtrude","CAP_FACE",FACE,{"disambiguationData":[OSD([subQ7,sQuery(id+"F27.wireOp",EDGE,"E95"),sQuery(id+"F27.wireOp",EDGE,"E96"),sQuery(id+"F27.wireOp",EDGE,"E97")])],"isStart":true}),makeQuery(id+"F28.opExtrude","CAP_FACE",FACE,{"disambiguationData":[OSD([subQ6,sQuery(id+"F27.wireOp",EDGE,"E99"),sQuery(id+"F27.wireOp",EDGE,"E102"),sQuery(id+"F27.wireOp",EDGE,"E103")])],"isStart":true}),makeQuery(id+"F28.opExtrude","CAP_FACE",FACE,{"disambiguationData":[OSD([subQ5,sQuery(id+"F27.wireOp",EDGE,"E110"),sQuery(id+"F27.wireOp",EDGE,"E111"),sQuery(id+"F27.wireOp",EDGE,"E112")])],"isStart":true}),makeQuery(id+"F28.opExtrude","CAP_FACE",FACE,{"disambiguationData":[OSD([subQ4,sQuery(id+"F27.wireOp",EDGE,"E113"),sQuery(id+"F27.wireOp",EDGE,"E114"),sQuery(id+"F27.wireOp",EDGE,"E115")])],"isStart":true}),makeQuery(id+"F28.opExtrude","CAP_FACE",FACE,{"disambiguationData":[OSD([subQ3,sQuery(id+"F27.wireOp",EDGE,"E117.MirrorCS"),sQuery(id+"F27.wireOp",EDGE,"E118.MirrorCS"),sQuery(id+"F27.wireOp",EDGE,"E119.MirrorCS")])],"isStart":true}),makeQuery(id+"F28.opExtrude","CAP_FACE",FACE,{"disambiguationData":[OSD([subQ2,sQuery(id+"F27.wireOp",EDGE,"E120.MirrorCS"),sQuery(id+"F27.wireOp",EDGE,"E121.MirrorCS"),sQuery(id+"F27.wireOp",EDGE,"E122.MirrorCS")])],"isStart":true}),makeQuery(id+"F28.opExtrude","CAP_FACE",FACE,{"disambiguationData":[OSD([subQ1,sQuery(id+"F27.wireOp",EDGE,"E123.MirrorCS"),sQuery(id+"F27.wireOp",EDGE,"E124.MirrorCS"),sQuery(id+"F27.wireOp",EDGE,"E125.MirrorCS")])],"isStart":true}),makeQuery(id+"F28.opExtrude","CAP_FACE",FACE,{"disambiguationData":[OSD([subQ0,sQuery(id+"F27.wireOp",EDGE,"E126.MirrorCS"),sQuery(id+"F27.wireOp",EDGE,"E127.MirrorCS"),sQuery(id+"F27.wireOp",EDGE,"E128.MirrorCS")])],"isStart":true})]});}
            var sketch = newSketch(context, id + "F29", { "sketchPlane" : qUnion([Q0])});
            skLineSegment(sketch, "E129.bottom", {"start": v(-4.26, 0) * mm, "end": v(5.2, 0) * mm});
            skLineSegment(sketch, "E129.left", {"start": v(-4.26, 0) * mm, "end": v(-4.26, -22.48) * mm});
            skLineSegment(sketch, "E129.right", {"start": v(5.2, 0) * mm, "end": v(5.2, -22.48) * mm});
            skLineSegment(sketch, "E130", {"start": v(5.2, -22.48) * mm, "end": v(4.11, -24.57) * mm});
            skLineSegment(sketch, "E131", {"start": v(4.11, -24.57) * mm, "end": v(-3.17, -24.57) * mm});
            skLineSegment(sketch, "E132", {"start": v(-3.17, -24.57) * mm, "end": v(-4.26, -22.48) * mm});
            skSolve(sketch);
        }
        {
            var Q0;
            {var subQ55=sQuery(id+"F29.wireOp",EDGE,"E129.bottom");Q0=makeQuery(id+"F29.imprint","IMPRINT",FACE,{"disambiguationData":[TD([[makeQuery(id+"F29.imprint","IMPRINT",EDGE,{"derivedFrom":subQ55}),1.0]])]});}
            extrude(context, id + "F30", {"entities" : qUnion([Q0]), "depth" : 5 * mm, "offsetDistance" : 25.4 * mm});
        }
        {
            var Q0;
            Q0=makeQuery(id+"F30.opExtrude","CAP_EDGE",EDGE,{"disambiguationData":[OSD([sQuery(id+"F29.wireOp",EDGE,"E129.right")])],"isStart":false});
            var Q1;
            Q1=makeQuery(id+"F30.opExtrude","CAP_EDGE",EDGE,{"disambiguationData":[OSD([sQuery(id+"F29.wireOp",EDGE,"E130")])],"isStart":false});
            var Q2;
            Q2=makeQuery(id+"F30.opExtrude","CAP_EDGE",EDGE,{"disambiguationData":[OSD([sQuery(id+"F29.wireOp",EDGE,"E131")])],"isStart":false});
            var Q3;
            Q3=makeQuery(id+"F30.opExtrude","CAP_EDGE",EDGE,{"disambiguationData":[OSD([sQuery(id+"F29.wireOp",EDGE,"E132")])],"isStart":false});
            var Q4;
            Q4=makeQuery(id+"F30.opExtrude","CAP_EDGE",EDGE,{"disambiguationData":[OSD([sQuery(id+"F29.wireOp",EDGE,"E129.left")])],"isStart":false});
            var Q5;
            Q5=makeQuery(id+"F30.opExtrude","CAP_EDGE",EDGE,{"disambiguationData":[OSD([sQuery(id+"F29.wireOp",EDGE,"E129.bottom")])],"isStart":false});
            chamfer(context, id + "F31", {"entities" : qUnion([Q0, Q1, Q2, Q3, Q4, Q5]), "chamferType" : ChamferType.OFFSET_ANGLE, "width" : 4 * mm, "oppositeDirection" : false, "angle" : 12 * degree, "tangentPropagation" : true});
        }
        {
            var Q0;
            {var subQ0=sQuery(id+"F0.wireOp",EDGE,"E0.right");var subQ1=sQuery(id+"F0.wireOp",EDGE,"E0.left");Q0=makeQuery(id+"F6.boolean.opBoolean","MERGE",FACE,{"derivedFrom":[makeQuery(id+"F1.opExtrude","CAP_FACE",FACE,{"disambiguationData":[OSD([sQuery(id+"F0.wireOp",EDGE,"E0.bottom"),subQ1,subQ0,sQuery(id+"F0.wireOp",EDGE,"E1"),sQuery(id+"F0.wireOp",EDGE,"E3.MirrorCS"),sQuery(id+"F0.wireOp",EDGE,"E4"),sQuery(id+"F0.wireOp",EDGE,"E5.MirrorCS"),sQuery(id+"F0.wireOp",EDGE,"E6")])],"isStart":false}),makeQuery(id+"F6.opExtrude","CAP_FACE",FACE,{"disambiguationData":[OSD([subQ1,sQuery(id+"F5.wireOp",EDGE,"E47")])],"isStart":true}),makeQuery(id+"F6.opExtrude","CAP_FACE",FACE,{"disambiguationData":[OSD([subQ0,sQuery(id+"F5.wireOp",EDGE,"E48.MirrorC")])],"isStart":true})]});}
            var sketch = newSketch(context, id + "F32", { "sketchPlane" : qUnion([Q0])});
            skCircle(sketch, "E133", {"center": v(-2.64, 0.13) * mm, "radius": 0.65 * mm});
            skCircle(sketch, "E134", {"center": v(3.58, 0.13) * mm, "radius": 0.65 * mm});
            skLineSegment(sketch, "E135", {"start": v(-2.64, 0.8) * mm, "end": v(3.58, 0.8) * mm});
            skLineSegment(sketch, "E136", {"start": v(3.58, -0.52) * mm, "end": v(3.58, -2.9) * mm});
            skLineSegment(sketch, "E137", {"start": v(-2.64, -0.52) * mm, "end": v(-2.64, -2.9) * mm});
            skCircle(sketch, "E138", {"center": v(3.58, -3.19) * mm, "radius": 2.2 * mm});
            skPoint(sketch, "E139", {"position": v(3.58, -3.62) * mm});
            skArc(sketch, "E140", {"start": v(3.58, -5.4) * mm, "mid": v(3.27, -6.93) * mm, "end": v(3.46, -8.48) * mm});
            skLineSegment(sketch, "E141", {"start": v(3.46, -8.48) * mm, "end": v(6.32, -11.28) * mm});
            skLineSegment(sketch, "E142", {"start": v(6.32, -11.28) * mm, "end": v(8.48, -14.2) * mm});
            skPoint(sketch, "E143", {"position": v(6.32, -11.28) * mm});
            skLineSegment(sketch, "E144", {"start": v(8.48, -14.2) * mm, "end": v(-7.54, -14.2) * mm});
            skLineSegment(sketch, "E145", {"start": v(-7.54, -14.2) * mm, "end": v(-5.38, -11.28) * mm});
            skArc(sketch, "E146", {"start": v(-2.64, -6.71) * mm, "mid": v(-2.22, -5.17) * mm, "end": v(-2.64, -3.62) * mm});
            skLineSegment(sketch, "E147", {"start": v(-5.38, -11.28) * mm, "end": v(-2.64, -6.71) * mm});
            skSolve(sketch);
        }
        {
            var Q0;
            {var subQ39=sQuery(id+"F32.wireOp",EDGE,"E134");Q0=makeQuery(id+"F32.imprint","IMPRINT",FACE,{"disambiguationData":[TD([[makeQuery(id+"F32.imprint","IMPRINT",EDGE,{"disambiguationData":[OD(0.0)],"derivedFrom":subQ39}),-1.0]])]});}
            extrude(context, id + "F33", {"entities" : qUnion([Q0]), "depth" : 2.57 * mm, "offsetDistance" : 25.4 * mm});
        }
        {
            var Q0;
            {var subQ0=sQuery(id+"F32.wireOp",EDGE,"E133");var subQ13=makeQuery(id+"F32.imprint","INTERSECT",VERTEX,{"derivedFrom":[subQ0,sQuery(id+"F32.wireOp",EDGE,"E137")]});Q0=makeQuery(id+"F32.imprint","IMPRINT",FACE,{"disambiguationData":[TD([[makeQuery(id+"F32.imprint","IMPRINT",EDGE,{"disambiguationData":[TD([[subQ13,1.0]])],"derivedFrom":subQ0}),1.0]])]});}
            var Q1;
            {var subQ0=sQuery(id+"F32.wireOp",EDGE,"E134");Q1=makeQuery(id+"F32.imprint","IMPRINT",FACE,{"disambiguationData":[TD([[makeQuery(id+"F32.imprint","IMPRINT",EDGE,{"disambiguationData":[OD(0.0)],"derivedFrom":subQ0}),1.0]])]});}
            extrude(context, id + "F34", {"entities" : qUnion([Q0, Q1]), "operationType" : NewBodyOperationType.ADD, "depth" : 2.8 * mm, "offsetDistance" : 25.4 * mm});
        }
        {
            var Q0;
            {var subQ0=sQuery(id+"F32.wireOp",EDGE,"E136");var subQ7=sQuery(id+"F32.wireOp",EDGE,"E138");var subQ8=makeQuery(id+"F32.imprint","INTERSECT",VERTEX,{"derivedFrom":[subQ0,subQ7]});Q0=makeQuery(id+"F32.imprint","IMPRINT",FACE,{"disambiguationData":[TD([[makeQuery(id+"F32.imprint","IMPRINT",EDGE,{"disambiguationData":[TD([[subQ8,-1.0]])],"derivedFrom":subQ0}),1.0]])]});}
            var Q1;
            {var subQ0=sQuery(id+"F32.wireOp",EDGE,"E136");var subQ7=sQuery(id+"F32.wireOp",EDGE,"E138");var subQ8=makeQuery(id+"F32.imprint","INTERSECT",VERTEX,{"derivedFrom":[subQ0,subQ7]});Q1=makeQuery(id+"F32.imprint","IMPRINT",FACE,{"disambiguationData":[TD([[makeQuery(id+"F32.imprint","IMPRINT",EDGE,{"disambiguationData":[TD([[subQ8,-1.0]])],"derivedFrom":subQ0}),-1.0]])]});}
            extrude(context, id + "F35", {"entities" : qUnion([Q0, Q1]), "operationType" : NewBodyOperationType.ADD, "depth" : 4 * mm, "offsetDistance" : 25.4 * mm});
        }
        {
            var Q0;
            Q0=makeQuery(id+"F33.opExtrude","SWEPT_FACE",FACE,{"disambiguationData":[OSD([sQuery(id+"F32.wireOp",EDGE,"E136")])]});
            var sketch = newSketch(context, id + "F36", { "sketchPlane" : qUnion([Q0])});
            skCircle(sketch, "E148", {"center": v(-23.29, -3.13) * mm, "radius": 1.27 * mm});
            skPoint(sketch, "E148.centerSnap0", {"position": v(-23.29, -0.98) * mm});
            skSolve(sketch);
        }
        {
            var Q0;
            Q0=makeQuery(id+"F36.imprint","IMPRINT",FACE,{"disambiguationData":[TD([[makeQuery(id+"F36.imprint","IMPRINT",EDGE,{"derivedFrom":sQuery(id+"F36.wireOp",EDGE,"E148")}),1.0]])]});
            extrude(context, id + "F37", {"entities" : qUnion([Q0]), "operationType" : NewBodyOperationType.ADD, "depth" : 6 * mm, "offsetDistance" : 25.4 * mm});
        }
        {
            var Q0;
            Q0=makeQuery(id+"F33.opExtrude","CAP_FACE",FACE,{"disambiguationData":[OSD([sQuery(id+"F0.wireOp",EDGE,"E0.left"),sQuery(id+"F0.wireOp",EDGE,"E0.right"),sQuery(id+"F32.wireOp",EDGE,"E133"),sQuery(id+"F32.wireOp",EDGE,"E134"),sQuery(id+"F32.wireOp",EDGE,"E135"),sQuery(id+"F32.wireOp",EDGE,"E136"),sQuery(id+"F32.wireOp",EDGE,"E137"),sQuery(id+"F32.wireOp",EDGE,"E138"),sQuery(id+"F32.wireOp",EDGE,"E140"),sQuery(id+"F32.wireOp",EDGE,"E141"),sQuery(id+"F32.wireOp",EDGE,"E142"),sQuery(id+"F32.wireOp",EDGE,"E144"),sQuery(id+"F32.wireOp",EDGE,"E145"),sQuery(id+"F32.wireOp",EDGE,"E146"),sQuery(id+"F32.wireOp",EDGE,"E147")])],"isStart":false});
            var sketch = newSketch(context, id + "F38", { "sketchPlane" : qUnion([Q0])});
            skArc(sketch, "E149", {"start": v(1.88, -4.58) * mm, "mid": v(-0.24, -3.44) * mm, "end": v(-2.64, -3.34) * mm});
            skArc(sketch, "E150", {"start": v(1.39, -3.34) * mm, "mid": v(-0.56, -2.61) * mm, "end": v(-2.64, -2.65) * mm});
            skLineSegment(sketch, "E151", {"start": v(-3.34, -1.68) * mm, "end": v(-2.64, -1.68) * mm});
            skArc(sketch, "E152", {"start": v(0.25, -1.01) * mm, "mid": v(1.16, -1.27) * mm, "end": v(2.05, -0.96) * mm});
            skLineSegment(sketch, "E153", {"start": v(0.25, -1.01) * mm, "end": v(-1.96, -1.01) * mm});
            skLineSegment(sketch, "E154", {"start": v(-1.96, -1.01) * mm, "end": v(-2.64, -1.01) * mm});
            skLineSegment(sketch, "E155", {"start": v(-2.64, -1.01) * mm, "end": v(-3.25, -1.01) * mm});
            skLineSegment(sketch, "E156", {"start": v(-3.25, -1.01) * mm, "end": v(-3.34, -1.68) * mm});
            skPoint(sketch, "E157", {"position": v(2.46, -0.77) * mm});
            skCircle(sketch, "E158", {"center": v(2.46, -0.77) * mm, "radius": 0.46 * mm});
            skArc(sketch, "E159", {"start": v(-2.2, -2.57) * mm, "mid": v(-2.14, -1.99) * mm, "end": v(-2.64, -1.68) * mm});
            skSolve(sketch);
        }
        {
            var Q0;
            {var subQ0=sQuery(id+"F38.wireOp",EDGE,"E149");Q0=makeQuery(id+"F38.imprint","IMPRINT",FACE,{"disambiguationData":[TD([[makeQuery(id+"F38.imprint","IMPRINT",EDGE,{"derivedFrom":subQ0}),-1.0]])]});}
            var Q1;
            {var subQ0=sQuery(id+"F38.wireOp",EDGE,"E153");Q1=makeQuery(id+"F38.imprint","IMPRINT",FACE,{"disambiguationData":[TD([[makeQuery(id+"F38.imprint","IMPRINT",EDGE,{"derivedFrom":subQ0}),1.0]])]});}
            var Q2;
            {var subQ0=sQuery(id+"F38.wireOp",EDGE,"E158");var subQ1=makeQuery(id+"F38.imprint","INTERSECT",VERTEX,{"derivedFrom":[sQuery(id+"F38.wireOp",EDGE,"E152"),subQ0]});Q2=makeQuery(id+"F38.imprint","IMPRINT",FACE,{"disambiguationData":[TD([[makeQuery(id+"F38.imprint","IMPRINT",EDGE,{"disambiguationData":[TD([[subQ1,-1.0]])],"derivedFrom":subQ0}),1.0]])]});}
            var Q3;
            {var subQ0=sQuery(id+"F38.wireOp",EDGE,"E151");Q3=makeQuery(id+"F38.imprint","IMPRINT",FACE,{"disambiguationData":[TD([[makeQuery(id+"F38.imprint","IMPRINT",EDGE,{"derivedFrom":subQ0}),1.0]])]});}
            extrude(context, id + "F39", {"entities" : qUnion([Q0, Q1, Q2, Q3]), "operationType" : NewBodyOperationType.ADD, "depth" : 1.45 * mm, "offsetDistance" : 25.4 * mm});
        }
        {
            var Q0;
            {var subQ0=sQuery(id+"F38.wireOp",EDGE,"E151");Q0=makeQuery(id+"F38.imprint","IMPRINT",FACE,{"disambiguationData":[TD([[makeQuery(id+"F38.imprint","IMPRINT",EDGE,{"derivedFrom":subQ0}),1.0]])]});}
            extrude(context, id + "F40", {"entities" : qUnion([Q0]), "operationType" : NewBodyOperationType.ADD, "oppositeDirection" : true, "depth" : 2.57 * mm, "offsetDistance" : 25.4 * mm});
        }
    });
